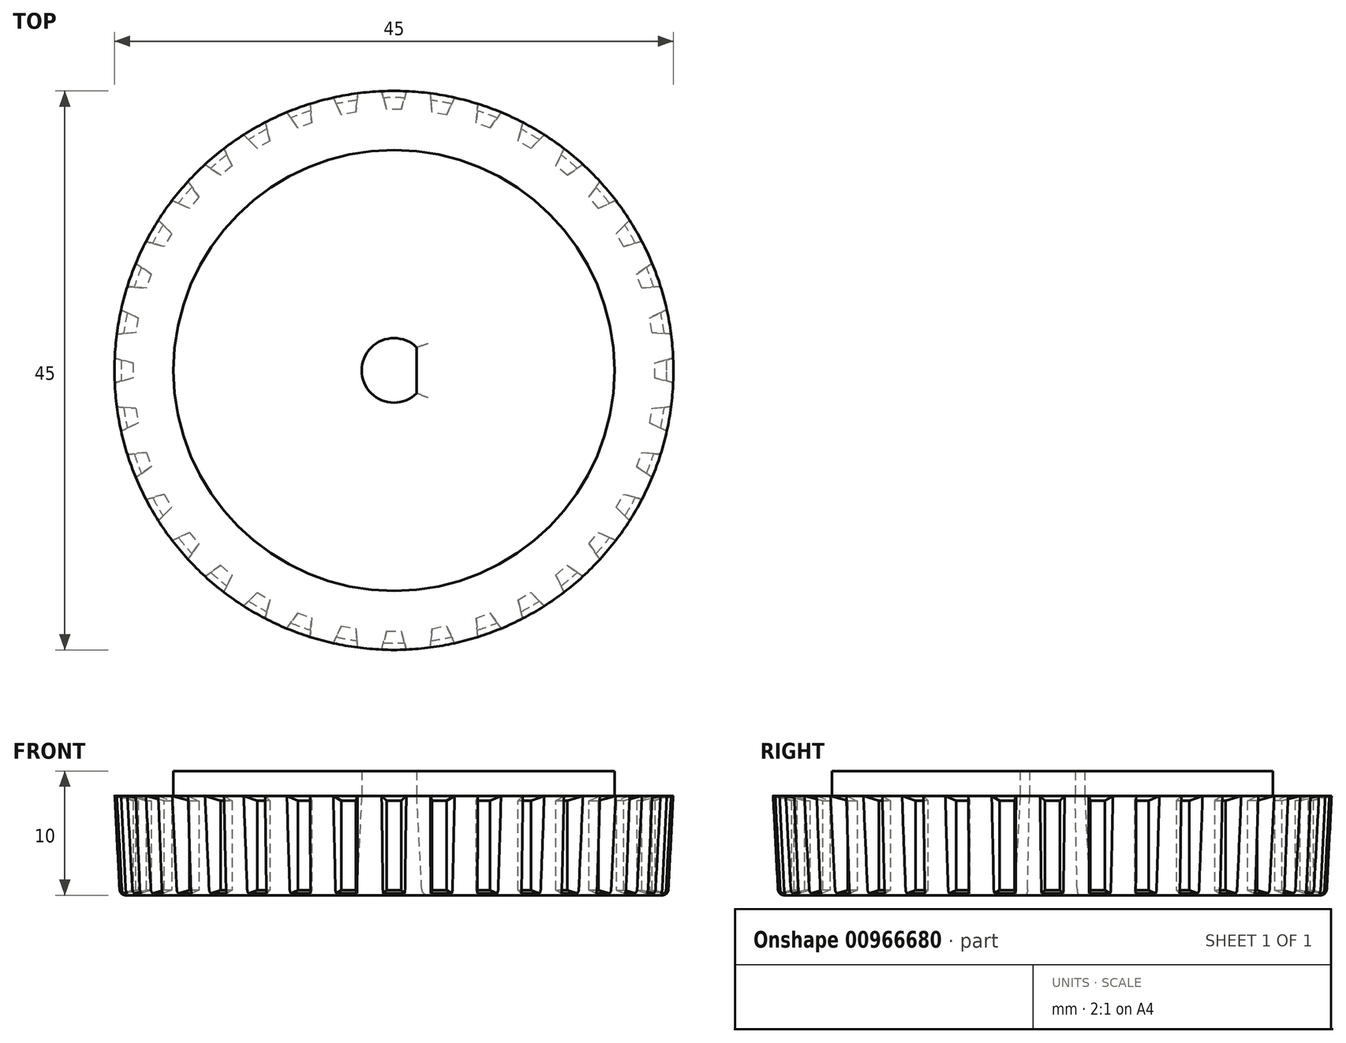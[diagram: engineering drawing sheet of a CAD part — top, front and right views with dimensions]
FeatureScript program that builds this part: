
annotation { "Feature Type Name" : "Feature", "Feature Type Description" : "" }
export const myFeature = defineFeature(function(context is Context, id is Id, definition is map)
    precondition{}
    {
        {
            var Q0;
            Q0=qCreatedBy(makeId("Top.planeOp"),FACE);
            var sketch = newSketch(context, id + "F0", { "sketchPlane" : qUnion([Q0])});
            skCircle(sketch, "E0", {"center": v(0, 0) * mm, "radius": 17.75 * mm});
            skArc(sketch, "E1", {"start": v(1.84, 1.84) * mm, "mid": v(-2.6, 0) * mm, "end": v(1.84, -1.84) * mm});
            skLineSegment(sketch, "E2", {"start": v(0, 0) * mm, "end": v(1.84, 1.84) * mm, "construction": true});
            skLineSegment(sketch, "E3", {"start": v(0, 0) * mm, "end": v(1.84, -1.84) * mm, "construction": true});
            skLineSegment(sketch, "E4", {"start": v(1.84, 1.84) * mm, "end": v(1.84, -1.84) * mm});
            skCircle(sketch, "E5", {"center": v(0, 0) * mm, "radius": 22.5 * mm});
            skLineSegment(sketch, "E6", {"start": v(0, -17.75) * mm, "end": v(0, 17.75) * mm});
            skLineSegment(sketch, "E7", {"start": v(0, 0) * mm, "end": v(22.5, 0) * mm, "construction": true});
            skLineSegment(sketch, "E8", {"start": v(22.5, 0) * mm, "end": v(28.5, 0) * mm, "construction": true});
            skLineSegment(sketch, "E9", {"start": v(28.5, 0) * mm, "end": v(16.3, -7.05) * mm});
            skLineSegment(sketch, "E10.MirrorCS", {"start": v(28.5, 0) * mm, "end": v(16.3, 7.05) * mm});
            skSolve(sketch);
        }
        {
            var Q0;
            {var subQ5=sQuery(id+"F0.wireOp",EDGE,"E6");var subQ6=sQuery(id+"F0.wireOp",EDGE,"E0");var subQ9=makeQuery(id+"F0.imprint","INTERSECT",VERTEX,{"disambiguationData":[OD(1.0)],"derivedFrom":[subQ6,subQ5]});Q0=makeQuery(id+"F0.imprint","IMPRINT",FACE,{"disambiguationData":[TD([[makeQuery(id+"F0.imprint","IMPRINT",EDGE,{"disambiguationData":[TD([[subQ9,1.0]])],"derivedFrom":subQ6}),-1.0]])]});}
            var Q1;
            {var subQ0=sQuery(id+"F0.wireOp",EDGE,"E6");var subQ1=sQuery(id+"F0.wireOp",EDGE,"E0");var subQ2=makeQuery(id+"F0.imprint","INTERSECT",VERTEX,{"disambiguationData":[OD(0.0)],"derivedFrom":[subQ1,subQ0]});Q1=makeQuery(id+"F0.imprint","IMPRINT",FACE,{"disambiguationData":[TD([[makeQuery(id+"F0.imprint","IMPRINT",EDGE,{"disambiguationData":[TD([[subQ2,1.0]])],"derivedFrom":subQ1}),1.0]])]});}
            var Q2;
            {var subQ0=sQuery(id+"F0.wireOp",EDGE,"E4");Q2=makeQuery(id+"F0.imprint","IMPRINT",FACE,{"disambiguationData":[TD([[makeQuery(id+"F0.imprint","IMPRINT",EDGE,{"derivedFrom":subQ0}),1.0]])]});}
            var Q3;
            {var subQ0=sQuery(id+"F0.wireOp",EDGE,"E9");var subQ1=sQuery(id+"F0.wireOp",EDGE,"E0");var subQ2=makeQuery(id+"F0.imprint","INTERSECT",VERTEX,{"derivedFrom":[subQ1,subQ0]});Q3=makeQuery(id+"F0.imprint","IMPRINT",FACE,{"disambiguationData":[TD([[makeQuery(id+"F0.imprint","IMPRINT",EDGE,{"disambiguationData":[TD([[subQ2,-1.0]])],"derivedFrom":subQ1}),-1.0]])]});}
            extrude(context, id + "F1", {"entities" : qUnion([Q0, Q1, Q2, Q3]), "oppositeDirection" : true, "depth" : 8 * mm, "offsetDistance" : 25 * mm, "hasDraft" : true, "draftAngle" : 3 * degree, "draftPullDirection" : true});
        }
        {
            var Q0;
            Q0=sQuery(id+"F0.wireOp",EDGE,"E7");
            var Q1;
            Q1=sQuery(id+"F0.wireOp",VERTEX,"E7.end");
            cPlane(context, id + "F2", {"entities" : qUnion([Q0, Q1]), "cplaneType" : CPlaneType.LINE_POINT, "offset" : 25 * mm, "width" : 150 * mm, "height" : 150 * mm});
        }
        {
            var Q0;
            Q0=qCreatedBy(id+"F2.planeOp",FACE);
            var sketch = newSketch(context, id + "F3", { "sketchPlane" : qUnion([Q0])});
            skLineSegment(sketch, "E11.bottom", {"start": v(-1, 0) * mm, "end": v(1, 0) * mm});
            skLineSegment(sketch, "E11.top", {"start": v(-1, -8) * mm, "end": v(1, -8) * mm});
            skLineSegment(sketch, "E11.left", {"start": v(-1, 0) * mm, "end": v(-1, -8) * mm});
            skLineSegment(sketch, "E11.right", {"start": v(1, 0) * mm, "end": v(1, -8) * mm});
            skLineSegment(sketch, "E12.bottom", {"start": v(1, 0) * mm, "end": v(-1, 0) * mm});
            skLineSegment(sketch, "E12.top", {"start": v(1, 2.69) * mm, "end": v(-1, 2.69) * mm});
            skLineSegment(sketch, "E12.left", {"start": v(1, 0) * mm, "end": v(1, 2.69) * mm});
            skLineSegment(sketch, "E12.right", {"start": v(-1, 0) * mm, "end": v(-1, 2.69) * mm});
            skLineSegment(sketch, "E13.bottom", {"start": v(1, -8) * mm, "end": v(-1, -8) * mm});
            skLineSegment(sketch, "E13.top", {"start": v(1, -10.57) * mm, "end": v(-1, -10.57) * mm});
            skLineSegment(sketch, "E13.left", {"start": v(1, -8) * mm, "end": v(1, -10.57) * mm});
            skLineSegment(sketch, "E13.right", {"start": v(-1, -8) * mm, "end": v(-1, -10.57) * mm});
            skSolve(sketch);
        }
        {
            var Q0;
            Q0=makeQuery(id+"F3.imprint","IMPRINT",FACE,{"disambiguationData":[TD([[makeQuery(id+"F3.imprint","IMPRINT",EDGE,{"derivedFrom":sQuery(id+"F3.wireOp",EDGE,"E11.left")}),1.0]])]});
            var Q1;
            Q1=makeQuery(id+"F3.imprint","IMPRINT",FACE,{"disambiguationData":[TD([[makeQuery(id+"F3.imprint","IMPRINT",EDGE,{"derivedFrom":sQuery(id+"F3.wireOp",EDGE,"E13.bottom")}),1.0]])]});
            var Q2;
            Q2=makeQuery(id+"F3.imprint","IMPRINT",FACE,{"disambiguationData":[TD([[makeQuery(id+"F3.imprint","IMPRINT",EDGE,{"derivedFrom":sQuery(id+"F3.wireOp",EDGE,"E12.bottom")}),-1.0]])]});
            extrude(context, id + "F4", {"entities" : qUnion([Q0, Q1, Q2]), "oppositeDirection" : true, "depth" : 1.5 * mm, "offsetDistance" : 25 * mm, "hasDraft" : true, "draftAngle" : 15 * degree, "draftPullDirection" : true});
        }
        {
            var Q0;
            Q0=makeQuery(id+"F0.imprint","IMPRINT",FACE,{"disambiguationData":[TD([[makeQuery(id+"F0.imprint","IMPRINT",EDGE,{"derivedFrom":sQuery(id+"F0.wireOp",EDGE,"E0")}),1.0]])]});
            var Q1;
            {var subQ0=sQuery(id+"F0.wireOp",EDGE,"E6");var subQ1=sQuery(id+"F0.wireOp",EDGE,"E0");var subQ2=makeQuery(id+"F0.imprint","INTERSECT",VERTEX,{"disambiguationData":[OD(0.0)],"derivedFrom":[subQ1,subQ0]});Q1=makeQuery(id+"F0.imprint","IMPRINT",FACE,{"disambiguationData":[TD([[makeQuery(id+"F0.imprint","IMPRINT",EDGE,{"disambiguationData":[TD([[subQ2,1.0]])],"derivedFrom":subQ1}),1.0]])]});}
            extrude(context, id + "F5", {"entities" : qUnion([Q0, Q1]), "operationType" : NewBodyOperationType.ADD, "depth" : 2 * mm, "offsetDistance" : 25 * mm});
        }
        {
            var Q0;
            Q0=makeQuery(id+"F4.opExtrude","SWEPT_BODY",BODY,{"disambiguationData":[OSD([sQuery(id+"F3.wireOp",EDGE,"E11.left"),sQuery(id+"F3.wireOp",EDGE,"E11.right"),sQuery(id+"F3.wireOp",EDGE,"E12.top"),sQuery(id+"F3.wireOp",EDGE,"E12.left"),sQuery(id+"F3.wireOp",EDGE,"E12.right"),sQuery(id+"F3.wireOp",EDGE,"E13.top"),sQuery(id+"F3.wireOp",EDGE,"E13.left"),sQuery(id+"F3.wireOp",EDGE,"E13.right")])]});
            var Q1;
            Q1=makeQuery(id+"F1.opExtrude","CAP_EDGE",EDGE,{"disambiguationData":[OSD([sQuery(id+"F0.wireOp",EDGE,"E5")])],"isStart":false});
            circularPattern(context, id + "F6", {"operationType" : NewBodyOperationType.REMOVE, "entities" : qUnion([Q0]), "axis" : qUnion([Q1]), "angle" : 360 * degree, "instanceCount" : 36, "equalSpace" : true});
        }
        {
            var Q0;
            Q0=makeQuery(id+"F1.opExtrude","CAP_FACE",FACE,{"disambiguationData":[OSD([sQuery(id+"F0.wireOp",EDGE,"E1"),sQuery(id+"F0.wireOp",EDGE,"E4"),sQuery(id+"F0.wireOp",EDGE,"E5")])],"isStart":false});
            fillet(context, id + "F7", {"entities" : qUnion([Q0]), "radius" : 0.5 * mm, "tangentPropagation" : true, "allowEdgeOverflow" : false});
        }
    });
